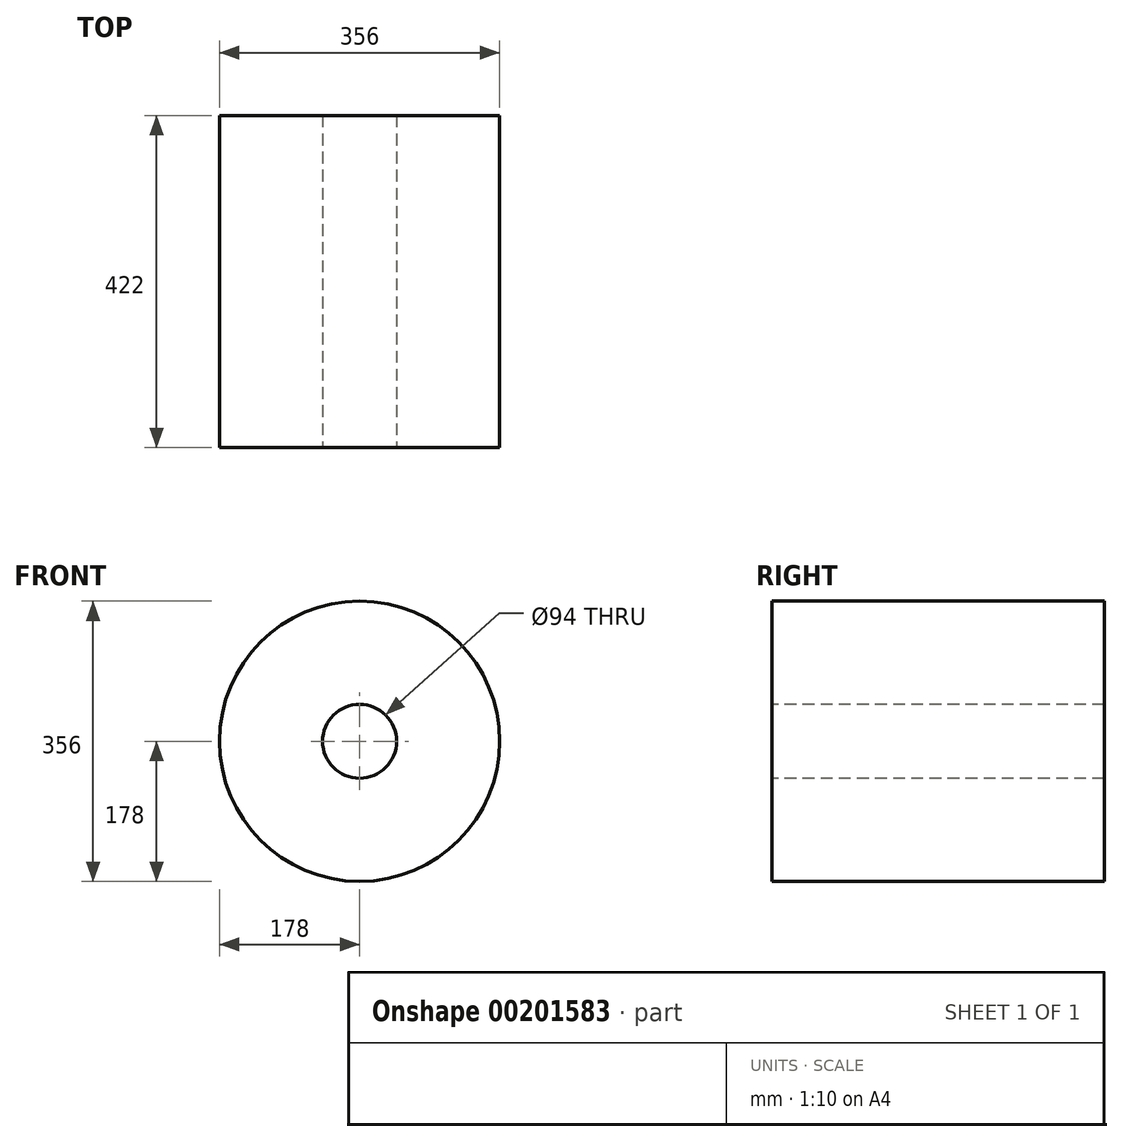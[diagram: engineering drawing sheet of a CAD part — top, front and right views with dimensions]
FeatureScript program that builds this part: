
annotation { "Feature Type Name" : "Feature", "Feature Type Description" : "" }
export const myFeature = defineFeature(function(context is Context, id is Id, definition is map)
    precondition{}
    {
        {
            var Q0;
            Q0=qCreatedBy(makeId("Front.planeOp"),FACE);
            var sketch = newSketch(context, id + "F0", { "sketchPlane" : qUnion([Q0])});
            skCircle(sketch, "E0", {"center": v(0, 0) * mm, "radius": 47 * mm});
            skCircle(sketch, "E1", {"center": v(0, 0) * mm, "radius": 178 * mm});
            skSolve(sketch);
        }
        {
            var Q0;
            Q0 = qSketchRegion(id + "F0", true);
            extrude(context, id + "F1", {"entities" : qUnion([Q0]), "oppositeDirection" : true, "depth" : 422 * mm});
        }
    });
